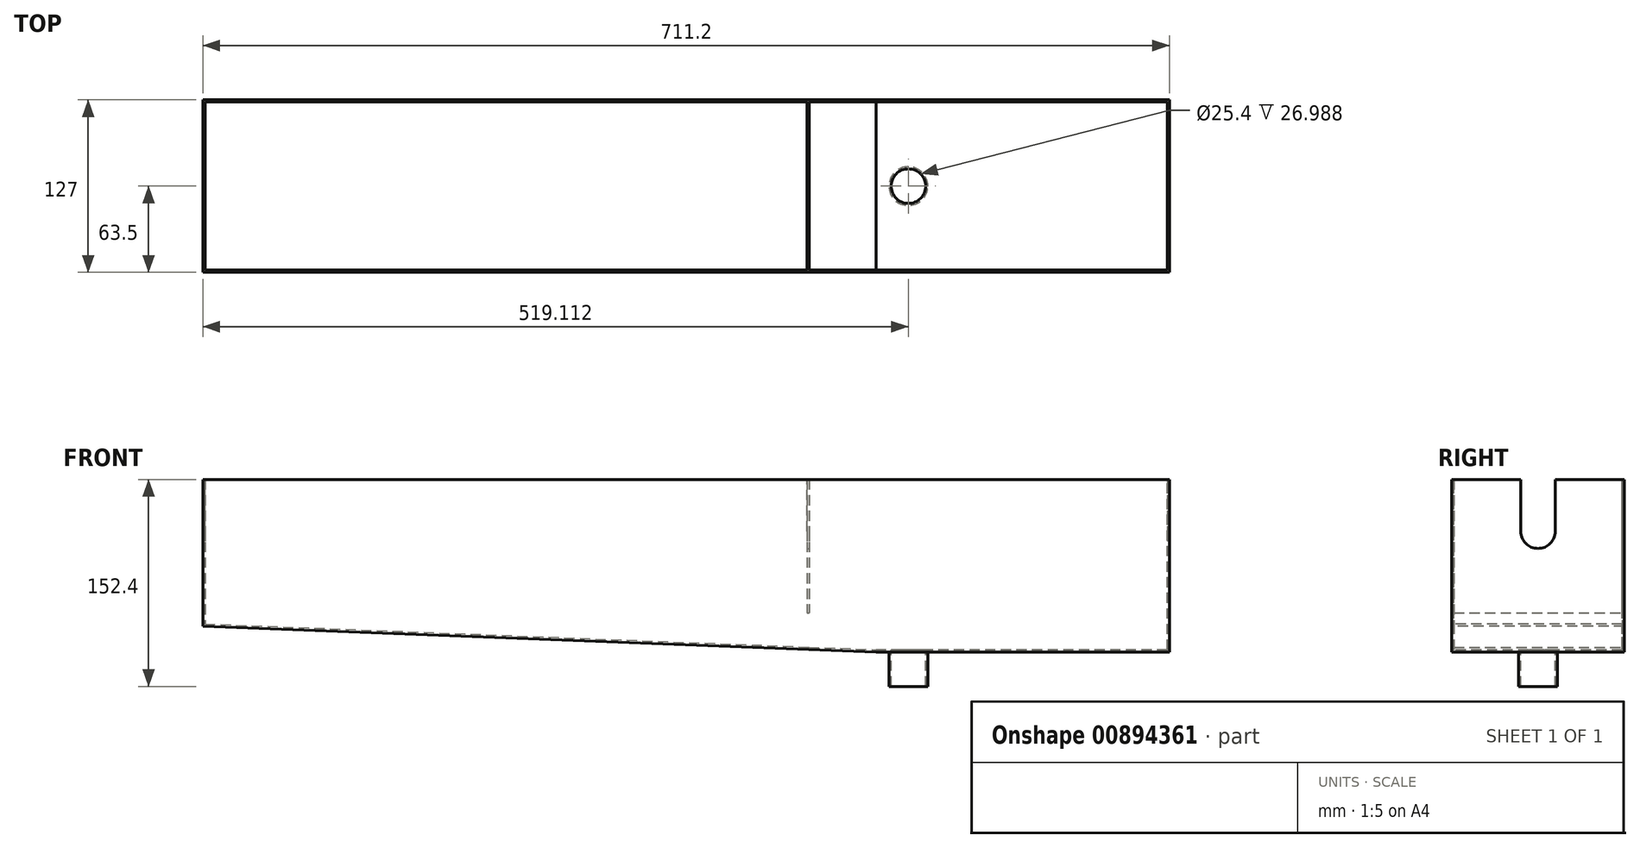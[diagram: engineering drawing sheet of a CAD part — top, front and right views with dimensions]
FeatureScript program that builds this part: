
annotation { "Feature Type Name" : "Feature", "Feature Type Description" : "" }
export const myFeature = defineFeature(function(context is Context, id is Id, definition is map)
    precondition{}
    {
        {
            var Q0;
            Q0=qCreatedBy(makeId("Front.planeOp"),FACE);
            var sketch = newSketch(context, id + "F0", { "sketchPlane" : qUnion([Q0])});
            skLineSegment(sketch, "E0", {"start": v(-355.6, 120.65) * mm, "end": v(355.6, 120.65) * mm});
            skLineSegment(sketch, "E1", {"start": v(355.6, 120.65) * mm, "end": v(355.6, -6.35) * mm});
            skLineSegment(sketch, "E2", {"start": v(355.6, -6.35) * mm, "end": v(139.7, -6.35) * mm});
            skLineSegment(sketch, "E3", {"start": v(-355.6, 120.65) * mm, "end": v(-355.6, 12.7) * mm});
            skLineSegment(sketch, "E4", {"start": v(-355.6, 12.7) * mm, "end": v(139.7, -6.35) * mm});
            skSolve(sketch);
        }
        {
            var Q0;
            Q0=makeQuery(id+"F0.imprint","IMPRINT",FACE,{"disambiguationData":[TD([[makeQuery(id+"F0.imprint","IMPRINT",EDGE,{"derivedFrom":sQuery(id+"F0.wireOp",EDGE,"E0")}),-1.0]])]});
            extrude(context, id + "F1", {"entities" : qUnion([Q0]), "oppositeDirection" : true, "depth" : 1.59 * mm, "offsetDistance" : 25.4 * mm});
        }
        {
            var Q0;
            Q0=makeQuery(id+"F1.opExtrude","SWEPT_FACE",FACE,{"disambiguationData":[OSD([sQuery(id+"F0.wireOp",EDGE,"E3")])]});
            var sketch = newSketch(context, id + "F2", { "sketchPlane" : qUnion([Q0])});
            skLineSegment(sketch, "E5", {"start": v(0, 120.65) * mm, "end": v(-127, 120.65) * mm});
            skLineSegment(sketch, "E6", {"start": v(0, 12.7) * mm, "end": v(-127, 12.7) * mm});
            skLineSegment(sketch, "E7", {"start": v(-127, 12.7) * mm, "end": v(-127, 120.65) * mm});
            skSolve(sketch);
        }
        {
            var Q0;
            {var subQ2=sQuery(id+"F2.wireOp",EDGE,"E7");Q0=makeQuery(id+"F2.imprint","IMPRINT",FACE,{"disambiguationData":[TD([[makeQuery(id+"F2.imprint","IMPRINT",EDGE,{"derivedFrom":subQ2}),-1.0]])]});}
            extrude(context, id + "F3", {"entities" : qUnion([Q0]), "operationType" : NewBodyOperationType.ADD, "oppositeDirection" : true, "depth" : 1.59 * mm, "offsetDistance" : 25.4 * mm});
        }
        {
            var Q0;
            Q0=makeQuery(id+"F1.opExtrude","SWEPT_FACE",FACE,{"disambiguationData":[OSD([sQuery(id+"F0.wireOp",EDGE,"E1")])]});
            var sketch = newSketch(context, id + "F4", { "sketchPlane" : qUnion([Q0])});
            skLineSegment(sketch, "E8", {"start": v(0, 120.65) * mm, "end": v(127, 120.65) * mm});
            skLineSegment(sketch, "E9", {"start": v(127, 120.65) * mm, "end": v(127, -6.35) * mm});
            skLineSegment(sketch, "E10", {"start": v(127, -6.35) * mm, "end": v(0, -6.35) * mm});
            skLineSegment(sketch, "E11", {"start": v(0, -6.35) * mm, "end": v(0, 120.65) * mm});
            skSolve(sketch);
        }
        {
            var Q0;
            Q0 = qSketchRegion(id + "F4", true);
            var Q1;
            {var subQ2=sQuery(id+"F4.wireOp",EDGE,"E9");Q1=makeQuery(id+"F4.imprint","IMPRINT",FACE,{"disambiguationData":[TD([[makeQuery(id+"F4.imprint","IMPRINT",EDGE,{"derivedFrom":subQ2}),-1.0]])]});}
            extrude(context, id + "F5", {"entities" : qUnion([Q0, Q1]), "operationType" : NewBodyOperationType.ADD, "oppositeDirection" : true, "depth" : 1.59 * mm, "offsetDistance" : 25.4 * mm});
        }
        {
            var Q0;
            Q0=makeQuery(id+"F3.opExtrude","SWEPT_FACE",FACE,{"disambiguationData":[OSD([sQuery(id+"F2.wireOp",EDGE,"E7")])]});
            var sketch = newSketch(context, id + "F6", { "sketchPlane" : qUnion([Q0])});
            skLineSegment(sketch, "E12", {"start": v(355.6, 120.65) * mm, "end": v(-355.6, 120.65) * mm});
            skLineSegment(sketch, "E13", {"start": v(-355.6, 120.65) * mm, "end": v(-355.6, -6.35) * mm});
            skLineSegment(sketch, "E14", {"start": v(355.6, 120.65) * mm, "end": v(355.6, 12.7) * mm});
            skLineSegment(sketch, "E15", {"start": v(-355.6, -6.35) * mm, "end": v(-139.7, -6.35) * mm});
            skLineSegment(sketch, "E16", {"start": v(-139.7, -6.35) * mm, "end": v(355.6, 12.7) * mm});
            skSolve(sketch);
        }
        {
            var Q0;
            Q0 = qSketchRegion(id + "F6", true);
            extrude(context, id + "F7", {"entities" : qUnion([Q0]), "operationType" : NewBodyOperationType.ADD, "oppositeDirection" : true, "depth" : 1.59 * mm, "offsetDistance" : 25.4 * mm});
        }
        {
            var Q0;
            Q0=makeQuery(id+"F1.opExtrude","CAP_FACE",FACE,{"disambiguationData":[OSD([sQuery(id+"F0.wireOp",EDGE,"E0"),sQuery(id+"F0.wireOp",EDGE,"E1"),sQuery(id+"F0.wireOp",EDGE,"E2"),sQuery(id+"F0.wireOp",EDGE,"E3"),sQuery(id+"F0.wireOp",EDGE,"E4")])],"isStart":true});
            var sketch = newSketch(context, id + "F8", { "sketchPlane" : qUnion([Q0])});
            skLineSegment(sketch, "E17", {"start": v(-355.6, 12.7) * mm, "end": v(-355.6, 14.29) * mm});
            skLineSegment(sketch, "E18", {"start": v(355.6, -6.35) * mm, "end": v(355.6, -4.76) * mm});
            skLineSegment(sketch, "E19", {"start": v(-355.6, 14.29) * mm, "end": v(139.7, -4.76) * mm});
            skLineSegment(sketch, "E20", {"start": v(355.6, -4.76) * mm, "end": v(139.7, -4.76) * mm});
            skSolve(sketch);
        }
        {
            var Q0;
            Q0=makeQuery(id+"F8.imprint","IMPRINT",FACE,{"disambiguationData":[TD([[makeQuery(id+"F8.imprint","IMPRINT",EDGE,{"derivedFrom":sQuery(id+"F8.wireOp",EDGE,"E17")}),1.0]])]});
            extrude(context, id + "F9", {"entities" : qUnion([Q0]), "operationType" : NewBodyOperationType.ADD, "oppositeDirection" : true, "depth" : 127 * mm, "offsetDistance" : 25.4 * mm});
        }
        {
            var Q0;
            Q0=makeQuery(id+"F1.opExtrude","CAP_FACE",FACE,{"disambiguationData":[OSD([sQuery(id+"F0.wireOp",EDGE,"E0"),sQuery(id+"F0.wireOp",EDGE,"E1"),sQuery(id+"F0.wireOp",EDGE,"E2"),sQuery(id+"F0.wireOp",EDGE,"E3"),sQuery(id+"F0.wireOp",EDGE,"E4")])],"isStart":true});
            var sketch = newSketch(context, id + "F10", { "sketchPlane" : qUnion([Q0])});
            skLineSegment(sketch, "E21", {"start": v(88.9, 120.65) * mm, "end": v(88.9, -4.4) * mm});
            skLineSegment(sketch, "E22", {"start": v(88.9, 120.65) * mm, "end": v(90.49, 120.65) * mm});
            skLineSegment(sketch, "E23", {"start": v(90.49, 120.65) * mm, "end": v(90.49, -4.46) * mm});
            skLineSegment(sketch, "E24", {"start": v(90.49, 120.65) * mm, "end": v(88.9, 120.65) * mm});
            skLineSegment(sketch, "E25", {"start": v(88.9, -4.4) * mm, "end": v(90.49, -4.46) * mm});
            skSolve(sketch);
        }
        {
            var Q0;
            Q0 = qSketchRegion(id + "F10", true);
            extrude(context, id + "F11", {"entities" : qUnion([Q0]), "operationType" : NewBodyOperationType.ADD, "oppositeDirection" : true, "depth" : 127 * mm, "offsetDistance" : 25.4 * mm});
        }
        {
            var Q0;
            Q0=makeQuery(id+"F5.boolean.opBoolean","MERGE",FACE,{"derivedFrom":[makeQuery(id+"F1.opExtrude","SWEPT_FACE",FACE,{"disambiguationData":[OSD([sQuery(id+"F0.wireOp",EDGE,"E1")])]}),makeQuery(id+"F5.opExtrude","CAP_FACE",FACE,{"disambiguationData":[OSD([sQuery(id+"F4.wireOp",EDGE,"E8"),sQuery(id+"F4.wireOp",EDGE,"E9"),sQuery(id+"F4.wireOp",EDGE,"E10"),sQuery(id+"F4.wireOp",EDGE,"E11")])],"isStart":true})]});
            var sketch = newSketch(context, id + "F12", { "sketchPlane" : qUnion([Q0])});
            skArc(sketch, "E26", {"start": v(50.8, 82.55) * mm, "mid": v(63.5, 69.85) * mm, "end": v(76.2, 82.55) * mm});
            skLineSegment(sketch, "E27", {"start": v(63.5, 120.65) * mm, "end": v(50.8, 120.65) * mm});
            skLineSegment(sketch, "E28", {"start": v(50.8, 120.65) * mm, "end": v(50.8, 82.55) * mm});
            skLineSegment(sketch, "E29", {"start": v(76.2, 82.55) * mm, "end": v(76.2, 120.65) * mm});
            skLineSegment(sketch, "E30", {"start": v(76.2, 120.65) * mm, "end": v(63.5, 120.65) * mm});
            skSolve(sketch);
        }
        {
            var Q0;
            Q0=makeQuery(id+"F12.imprint","IMPRINT",FACE,{"disambiguationData":[TD([[makeQuery(id+"F12.imprint","IMPRINT",EDGE,{"derivedFrom":sQuery(id+"F12.wireOp",EDGE,"E26")}),1.0]])]});
            extrude(context, id + "F13", {"entities" : qUnion([Q0]), "operationType" : NewBodyOperationType.REMOVE, "endBound" : BoundingType.THROUGH_ALL, "oppositeDirection" : true, "depth" : 25.4 * mm, "offsetDistance" : 25.4 * mm});
        }
        {
            var Q0;
            Q0=makeQuery(id+"F9.opExtrude","SWEPT_FACE",FACE,{"disambiguationData":[OSD([sQuery(id+"F8.wireOp",EDGE,"E20")])]});
            var sketch = newSketch(context, id + "F14", { "sketchPlane" : qUnion([Q0])});
            skLineSegment(sketch, "E31", {"start": v(354.01, 63.5) * mm, "end": v(163.51, 63.5) * mm});
            skCircle(sketch, "E32", {"center": v(163.51, 63.5) * mm, "radius": 12.7 * mm});
            skSolve(sketch);
        }
        {
            var Q0;
            Q0=makeQuery(id+"F14.imprint","IMPRINT",FACE,{"disambiguationData":[TD([[makeQuery(id+"F14.imprint","IMPRINT",EDGE,{"derivedFrom":sQuery(id+"F14.wireOp",EDGE,"E32")}),1.0]])]});
            extrude(context, id + "F15", {"entities" : qUnion([Q0]), "operationType" : NewBodyOperationType.REMOVE, "oppositeDirection" : true, "depth" : 25.4 * mm, "offsetDistance" : 25.4 * mm});
        }
        {
            var Q0;
            {var subQ0=sQuery(id+"F0.wireOp",EDGE,"E2");Q0=makeQuery(id+"F9.boolean.opBoolean","MERGE",FACE,{"derivedFrom":[makeQuery(id+"F7.boolean.opBoolean","MERGE",FACE,{"derivedFrom":[makeQuery(id+"F5.boolean.opBoolean","MERGE",FACE,{"derivedFrom":[makeQuery(id+"F1.opExtrude","SWEPT_FACE",FACE,{"disambiguationData":[OSD([subQ0])]}),makeQuery(id+"F5.opExtrude","SWEPT_FACE",FACE,{"disambiguationData":[OSD([sQuery(id+"F4.wireOp",EDGE,"E10")])]})]}),makeQuery(id+"F7.opExtrude","SWEPT_FACE",FACE,{"disambiguationData":[OSD([sQuery(id+"F6.wireOp",EDGE,"E15")])]})]}),makeQuery(id+"F9.opExtrude","SWEPT_FACE",FACE,{"disambiguationData":[OSD([subQ0])]})]});}
            var sketch = newSketch(context, id + "F16", { "sketchPlane" : qUnion([Q0])});
            skCircle(sketch, "E33", {"center": v(163.51, -63.5) * mm, "radius": 14.29 * mm});
            skCircle(sketch, "E34", {"center": v(163.51, -63.5) * mm, "radius": 12.7 * mm});
            skSolve(sketch);
        }
        {
            var Q0;
            Q0=makeQuery(id+"F16.imprint","IMPRINT",FACE,{"disambiguationData":[TD([[makeQuery(id+"F16.imprint","IMPRINT",EDGE,{"derivedFrom":sQuery(id+"F16.wireOp",EDGE,"E33")}),1.0]])]});
            extrude(context, id + "F17", {"entities" : qUnion([Q0]), "operationType" : NewBodyOperationType.ADD, "depth" : 25.4 * mm, "offsetDistance" : 25.4 * mm});
        }
        {
            var Q0;
            Q0=makeQuery(id+"F11.opExtrude","SWEPT_FACE",FACE,{"disambiguationData":[OSD([sQuery(id+"F10.wireOp",EDGE,"E23")])]});
            var sketch = newSketch(context, id + "F18", { "sketchPlane" : qUnion([Q0])});
            skLineSegment(sketch, "E35", {"start": v(1.59, -2.87) * mm, "end": v(1.59, 22.53) * mm});
            skLineSegment(sketch, "E36", {"start": v(1.59, 22.53) * mm, "end": v(125.41, 22.53) * mm});
            skLineSegment(sketch, "E37", {"start": v(125.41, 22.53) * mm, "end": v(125.41, -2.87) * mm});
            skLineSegment(sketch, "E38", {"start": v(125.41, -2.87) * mm, "end": v(1.59, -2.87) * mm});
            skSolve(sketch);
        }
        {
            var Q0;
            Q0 = qSketchRegion(id + "F18", true);
            extrude(context, id + "F19", {"entities" : qUnion([Q0]), "operationType" : NewBodyOperationType.REMOVE, "oppositeDirection" : true, "depth" : 1.59 * mm, "offsetDistance" : 25.4 * mm});
        }
    });
